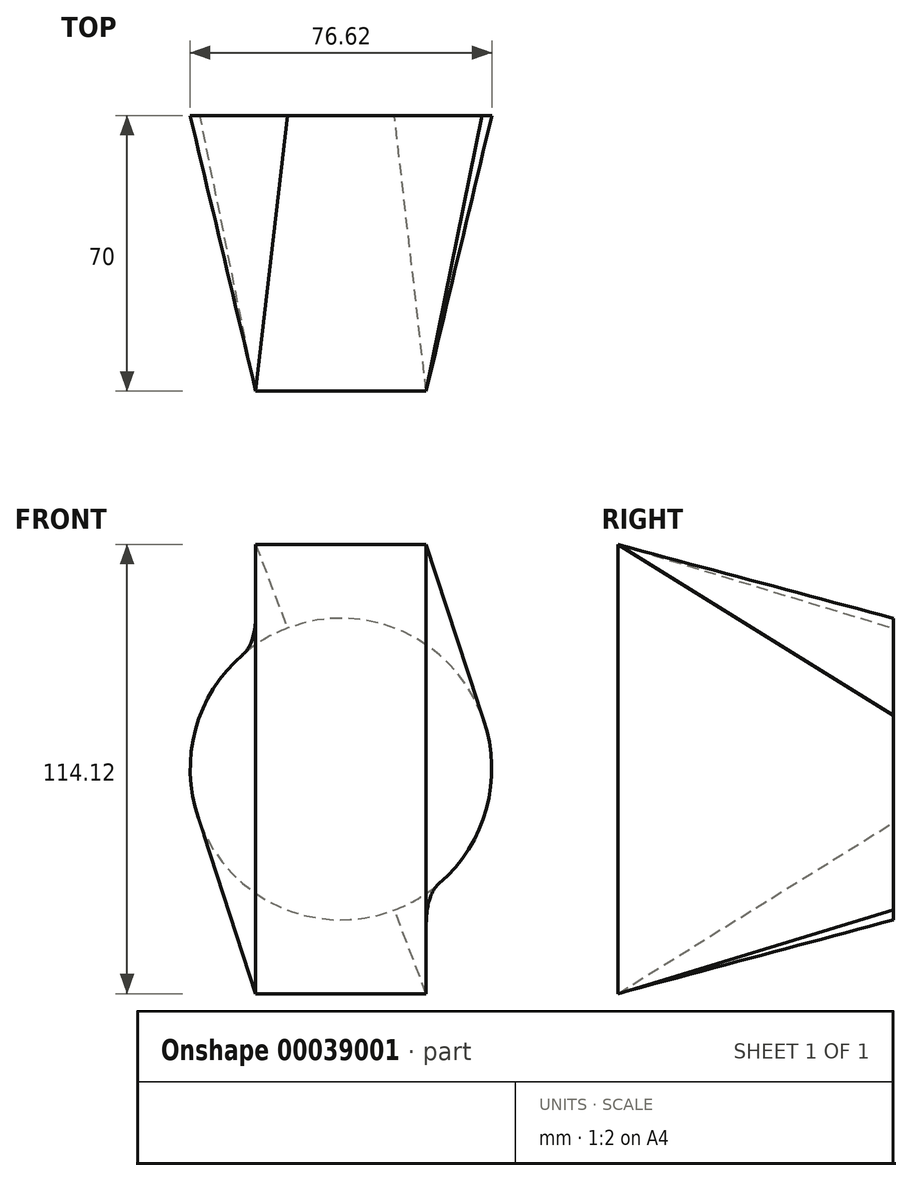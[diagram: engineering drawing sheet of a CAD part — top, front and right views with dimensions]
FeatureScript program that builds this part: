
annotation { "Feature Type Name" : "Feature", "Feature Type Description" : "" }
export const myFeature = defineFeature(function(context is Context, id is Id, definition is map)
    precondition{}
    {
        {
            var Q0;
            Q0=qCreatedBy(makeId("Front.planeOp"),FACE);
            var sketch = newSketch(context, id + "F0", { "sketchPlane" : qUnion([Q0])});
            skCircle(sketch, "E0", {"center": v(0, 0) * mm, "radius": 38.31 * mm});
            skSolve(sketch);
        }
        {
            var Q0;
            Q0=qCreatedBy(makeId("Front.planeOp"),FACE);
            cPlane(context, id + "F1", {"entities" : qUnion([Q0]), "cplaneType" : CPlaneType.OFFSET, "offset" : 70 * mm, "width" : 150 * mm, "height" : 150 * mm});
        }
        {
            var Q0;
            Q0=qCreatedBy(id+"F1.planeOp",FACE);
            var sketch = newSketch(context, id + "F2", { "sketchPlane" : qUnion([Q0])});
            skLineSegment(sketch, "E1.rect.bottom", {"start": v(-21.65, 57.06) * mm, "end": v(21.65, 57.06) * mm});
            skLineSegment(sketch, "E1.rect.top", {"start": v(-21.65, -57.06) * mm, "end": v(21.65, -57.06) * mm});
            skLineSegment(sketch, "E1.rect.left", {"start": v(-21.65, 57.06) * mm, "end": v(-21.65, -57.06) * mm});
            skLineSegment(sketch, "E1.rect.right", {"start": v(21.65, 57.06) * mm, "end": v(21.65, -57.06) * mm});
            skPoint(sketch, "E1.rect.middle", {"position": v(0, 0) * mm});
            skSolve(sketch);
        }
        {
            var Q0;
            Q0 = qSketchRegion(id + "F2", true);
            var Q1;
            Q1 = qSketchRegion(id + "F0", true);
            loft(context, id + "F3", {"sheetProfilesArray" : [{ "sheetProfileEntities" : qUnion([Q0]) }, { "sheetProfileEntities" : qUnion([Q1]) }]});
        }
    });
